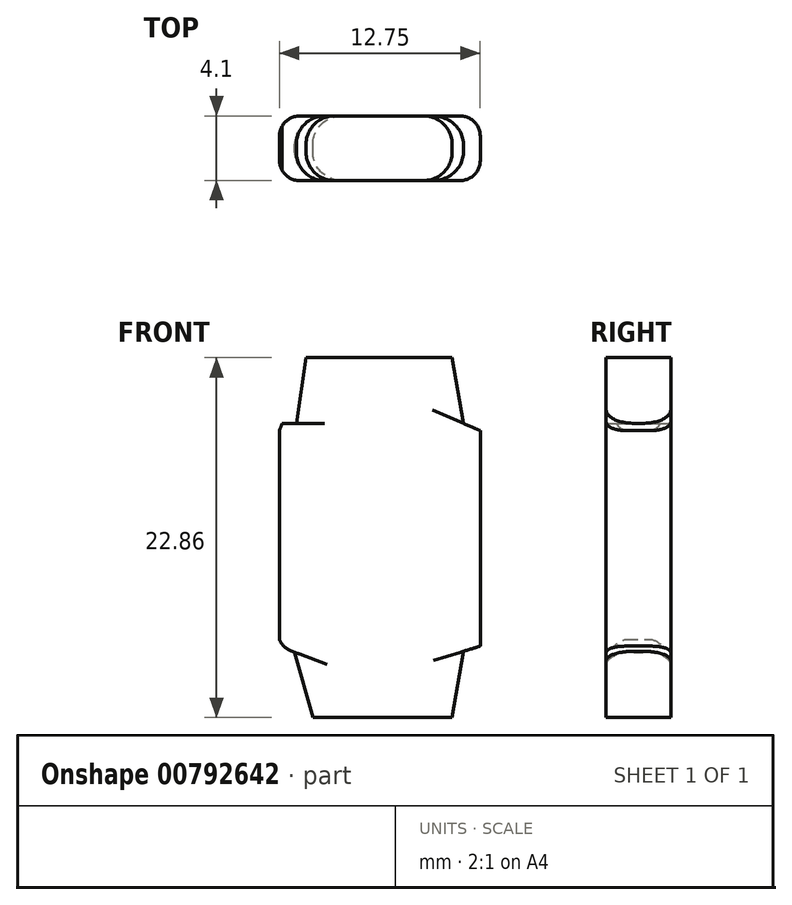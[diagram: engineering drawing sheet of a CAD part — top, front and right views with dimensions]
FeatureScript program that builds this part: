
annotation { "Feature Type Name" : "Feature", "Feature Type Description" : "" }
export const myFeature = defineFeature(function(context is Context, id is Id, definition is map)
    precondition{}
    {
        {
            var Q0;
            Q0=qCreatedBy(makeId("Front.planeOp"),FACE);
            var sketch = newSketch(context, id + "F0", { "sketchPlane" : qUnion([Q0])});
            skFitSpline(sketch, "E0.0", {"points": [v(9.65, 4.85) * mm, v(7.43, 4.85) * mm, v(5.22, 4.85) * mm, v(3, 4.85) * mm]});
            skLineSegment(sketch, "E1.0", {"start": v(10.96, 4.85) * mm, "end": v(9.65, 4.85) * mm});
            skLineSegment(sketch, "E2.0", {"start": v(3, 4.85) * mm, "end": v(1.7, 4.85) * mm});
            skFitSpline(sketch, "E3.0", {"points": [v(9.65, -18) * mm, v(7.59, -18) * mm, v(5.53, -18) * mm, v(3.47, -18) * mm]});
            skLineSegment(sketch, "E4.0", {"start": v(3.47, -18) * mm, "end": v(2.12, -18) * mm});
            skLineSegment(sketch, "E5.0", {"start": v(9.65, -18) * mm, "end": v(10.96, -18) * mm});
            skLineSegment(sketch, "E6.0", {"start": v(11.68, -13.8) * mm, "end": v(10.96, -18) * mm});
            skLineSegment(sketch, "E7.0", {"start": v(2.12, -18) * mm, "end": v(0.96, -13.86) * mm});
            skLineSegment(sketch, "E8", {"start": v(11.68, -13.8) * mm, "end": v(12.75, -13.48) * mm});
            skLineSegment(sketch, "E9", {"start": v(12.75, -13.48) * mm, "end": v(12.75, 0.21) * mm});
            skLineSegment(sketch, "E10", {"start": v(11.68, 0.68) * mm, "end": v(12.75, 0.21) * mm});
            skLineSegment(sketch, "E11", {"start": v(10.96, 4.85) * mm, "end": v(11.68, 0.68) * mm});
            skLineSegment(sketch, "E12", {"start": v(1.07, 0.67) * mm, "end": v(0.17, 0.67) * mm});
            skLineSegment(sketch, "E13", {"start": v(0, 0.23) * mm, "end": v(0.17, 0.67) * mm});
            skEllipticalArc(sketch, "E14.0", {});
            skLineSegment(sketch, "E15", {"start": v(0, 0.23) * mm, "end": v(0, -13.06) * mm});
            skLineSegment(sketch, "E16", {"start": v(0.72, -13.77) * mm, "end": v(0.96, -13.86) * mm});
            skLineSegment(sketch, "E17", {"start": v(1.07, 0.67) * mm, "end": v(1.7, 4.85) * mm});
            const initialGuessF0  = {"E14.0": [0.001179494284744654, -0.01256197143715383, -0.3536529577131228, -0.9353767078032038, 0.001295399986217654, 0.0012658553842754194, 5.460555721223327, 0]};
            skSetInitialGuess(sketch, initialGuessF0);
            skSolve(sketch);
        }
        {
            var Q0;
            Q0 = qSketchRegion(id + "F0", true);
            extrude(context, id + "F1", {"entities" : qUnion([Q0]), "endBound" : BoundingType.SYMMETRIC, "depth" : 4.1 * mm, "offsetDistance" : 25.4 * mm});
        }
        {
            var Q0;
            Q0=makeQuery(id+"F1.opExtrude","CAP_EDGE",EDGE,{"disambiguationData":[OSD([sQuery(id+"F0.wireOp",EDGE,"E17")])],"isStart":false});
            var Q1;
            Q1=makeQuery(id+"F1.opExtrude","CAP_EDGE",EDGE,{"disambiguationData":[OSD([sQuery(id+"F0.wireOp",EDGE,"E17")])],"isStart":true});
            var Q2;
            Q2=makeQuery(id+"F1.opExtrude","CAP_EDGE",EDGE,{"disambiguationData":[OSD([sQuery(id+"F0.wireOp",EDGE,"E11")])],"isStart":false});
            var Q3;
            Q3=makeQuery(id+"F1.opExtrude","CAP_EDGE",EDGE,{"disambiguationData":[OSD([sQuery(id+"F0.wireOp",EDGE,"E11")])],"isStart":true});
            var Q4;
            Q4=makeQuery(id+"F1.opExtrude","CAP_EDGE",EDGE,{"disambiguationData":[OSD([sQuery(id+"F0.wireOp",EDGE,"E6.0")])],"isStart":false});
            var Q5;
            Q5=makeQuery(id+"F1.opExtrude","CAP_EDGE",EDGE,{"disambiguationData":[OSD([sQuery(id+"F0.wireOp",EDGE,"E7.0")])],"isStart":false});
            var Q6;
            Q6=makeQuery(id+"F1.opExtrude","CAP_EDGE",EDGE,{"disambiguationData":[OSD([sQuery(id+"F0.wireOp",EDGE,"E6.0")])],"isStart":true});
            var Q7;
            Q7=makeQuery(id+"F1.opExtrude","CAP_EDGE",EDGE,{"disambiguationData":[OSD([sQuery(id+"F0.wireOp",EDGE,"E7.0")])],"isStart":true});
            fillet(context, id + "F2", {"entities" : qUnion([Q0, Q1, Q2, Q3, Q4, Q5, Q6, Q7]), "radius" : 1.78 * mm, "tangentPropagation" : true, "allowEdgeOverflow" : false});
        }
        {
            var Q0;
            Q0=makeQuery(id+"F1.opExtrude","CAP_EDGE",EDGE,{"disambiguationData":[OSD([sQuery(id+"F0.wireOp",EDGE,"E15")])],"isStart":false});
            var Q1;
            Q1=makeQuery(id+"F1.opExtrude","CAP_EDGE",EDGE,{"disambiguationData":[OSD([sQuery(id+"F0.wireOp",EDGE,"E15")])],"isStart":true});
            var Q2;
            Q2=makeQuery(id+"F1.opExtrude","CAP_EDGE",EDGE,{"disambiguationData":[OSD([sQuery(id+"F0.wireOp",EDGE,"E9")])],"isStart":true});
            var Q3;
            Q3=makeQuery(id+"F1.opExtrude","CAP_EDGE",EDGE,{"disambiguationData":[OSD([sQuery(id+"F0.wireOp",EDGE,"E9")])],"isStart":false});
            fillet(context, id + "F3", {"entities" : qUnion([Q0, Q1, Q2, Q3]), "radius" : 1.27 * mm, "tangentPropagation" : true, "allowEdgeOverflow" : false});
        }
    });
